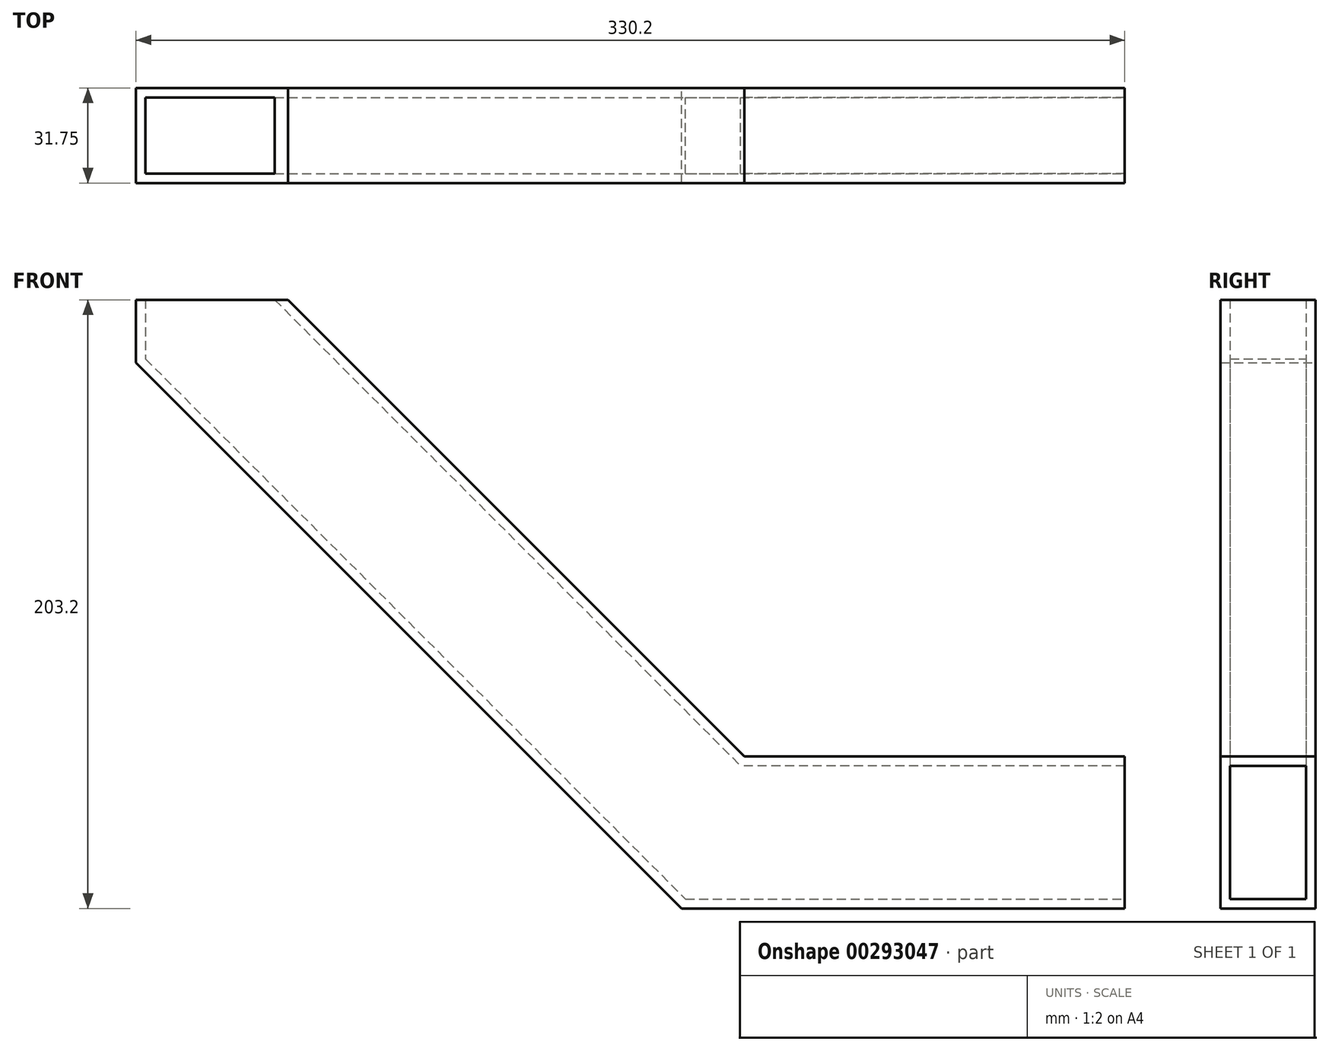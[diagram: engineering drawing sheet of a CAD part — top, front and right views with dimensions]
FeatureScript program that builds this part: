
annotation { "Feature Type Name" : "Feature", "Feature Type Description" : "" }
export const myFeature = defineFeature(function(context is Context, id is Id, definition is map)
    precondition{}
    {
        {
            var Q0;
            Q0=qCreatedBy(makeId("Front.planeOp"),FACE);
            var sketch = newSketch(context, id + "F0", { "sketchPlane" : qUnion([Q0])});
            skLineSegment(sketch, "E0", {"start": v(0, 0) * mm, "end": v(0, -21.04) * mm});
            skLineSegment(sketch, "E1", {"start": v(182.16, -203.2) * mm, "end": v(330.2, -203.2) * mm});
            skLineSegment(sketch, "E2", {"start": v(330.2, -203.2) * mm, "end": v(330.2, -152.4) * mm});
            skLineSegment(sketch, "E3", {"start": v(330.2, -152.4) * mm, "end": v(203.2, -152.4) * mm});
            skLineSegment(sketch, "E4", {"start": v(50.8, 0) * mm, "end": v(50.8, 0) * mm});
            skLineSegment(sketch, "E5", {"start": v(50.8, 0) * mm, "end": v(0, 0) * mm});
            skPoint(sketch, "E6.visualSharp", {"position": v(50.8, -152.4) * mm});
            skPoint(sketch, "E7.visualSharp", {"position": v(0, -203.2) * mm});
            skLineSegment(sketch, "E8", {"start": v(50.8, 0) * mm, "end": v(203.2, -152.4) * mm});
            skLineSegment(sketch, "E9", {"start": v(0, -21.04) * mm, "end": v(182.16, -203.2) * mm});
            skSolve(sketch);
        }
        {
            var Q0;
            Q0=makeQuery(id+"F0.imprint","IMPRINT",FACE,{"disambiguationData":[TD([[makeQuery(id+"F0.imprint","IMPRINT",EDGE,{"derivedFrom":sQuery(id+"F0.wireOp",EDGE,"E0")}),1.0]])]});
            extrude(context, id + "F1", {"entities" : qUnion([Q0]), "depth" : 31.75 * mm});
        }
        {
            var Q0;
            Q0=makeQuery(id+"F1.opExtrude","SWEPT_FACE",FACE,{"disambiguationData":[OSD([sQuery(id+"F0.wireOp",EDGE,"E5")])]});
            var Q1;
            Q1=makeQuery(id+"F1.opExtrude","SWEPT_FACE",FACE,{"disambiguationData":[OSD([sQuery(id+"F0.wireOp",EDGE,"E2")])]});
            shell(context, id + "F2", {"entities" : qUnion([Q0, Q1]), "thickness" : 3.17 * mm});
        }
    });
